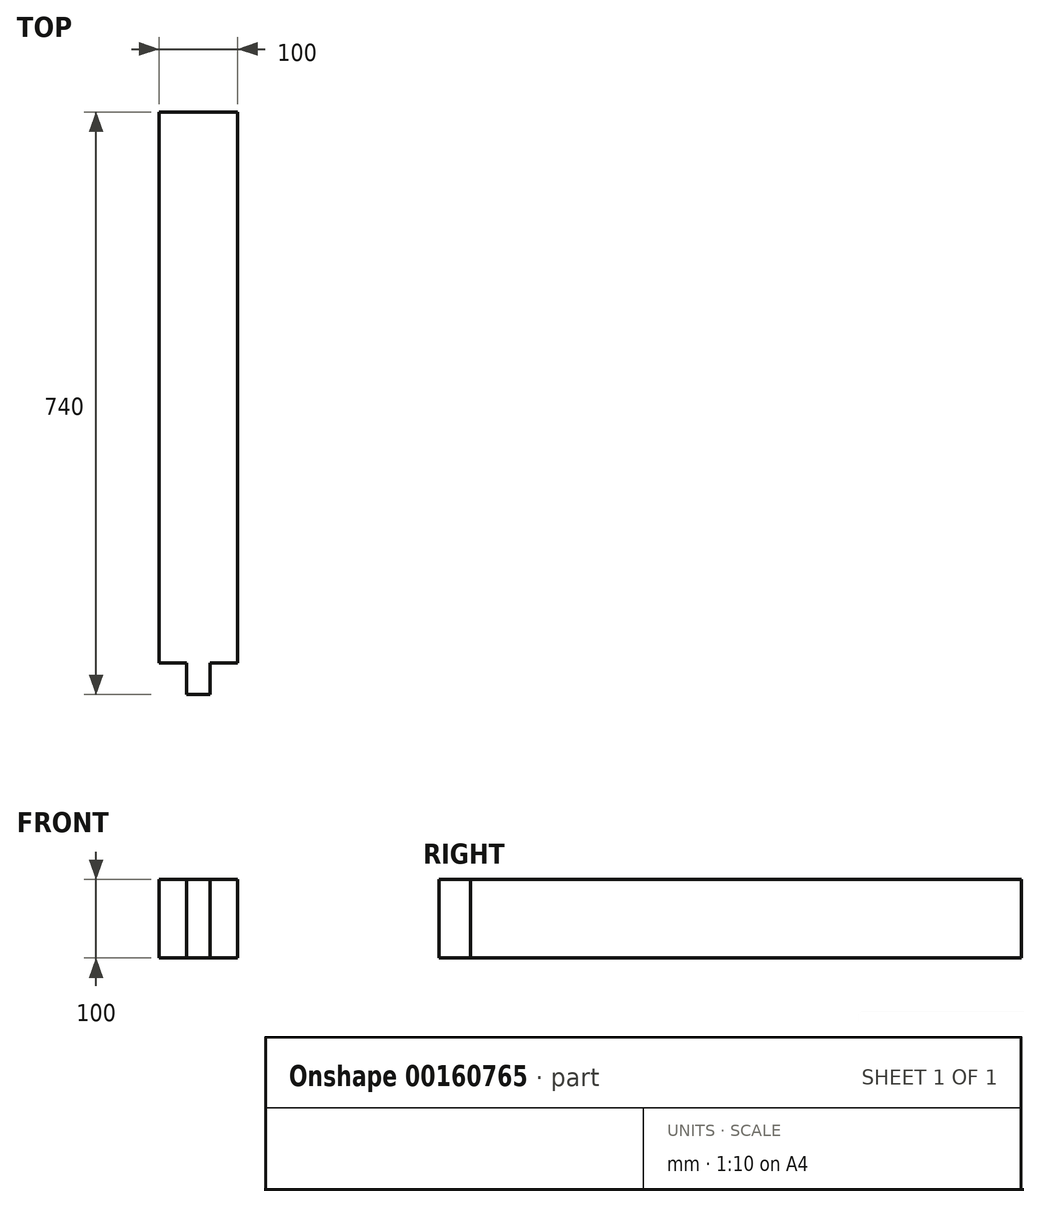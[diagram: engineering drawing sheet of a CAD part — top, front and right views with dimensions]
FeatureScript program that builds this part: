
annotation { "Feature Type Name" : "Feature", "Feature Type Description" : "" }
export const myFeature = defineFeature(function(context is Context, id is Id, definition is map)
    precondition{}
    {
        {
            assignVariable(context, id + "F0", {"name" : "L", "anyValue" : 600 * mm + 100 * mm});
        }
        {
            assignVariable(context, id + "F1", {"name" : "t_Feder", "anyValue" : 40 * mm});
        }
        {
            var Q0;
            Q0=qCreatedBy(makeId("Front.planeOp"),FACE);
            var sketch = newSketch(context, id + "F2", { "sketchPlane" : qUnion([Q0])});
            skLineSegment(sketch, "E0.bottom", {"start": v(50, -50) * mm, "end": v(-50, -50) * mm});
            skLineSegment(sketch, "E0.top", {"start": v(50, 50) * mm, "end": v(-50, 50) * mm});
            skLineSegment(sketch, "E0.left", {"start": v(50, -50) * mm, "end": v(50, 50) * mm});
            skLineSegment(sketch, "E0.right", {"start": v(-50, -50) * mm, "end": v(-50, 50) * mm});
            skPoint(sketch, "E0.middle", {"position": v(0, 0) * mm});
            skSolve(sketch);
        }
        {
            var Q0;
            Q0 = qSketchRegion(id + "F2", true);
            extrude(context, id + "F3", {"entities" : qUnion([Q0]), "endBound" : BoundingType.SYMMETRIC, "depth" : getVariable(context, 'L')});
        }
        {
            var Q0;
            Q0=makeQuery(id+"F3.opExtrude","CAP_FACE",FACE,{"disambiguationData":[OSD([sQuery(id+"F2.wireOp",EDGE,"E0.bottom"),sQuery(id+"F2.wireOp",EDGE,"E0.top"),sQuery(id+"F2.wireOp",EDGE,"E0.left"),sQuery(id+"F2.wireOp",EDGE,"E0.right")])],"isStart":false});
            var sketch = newSketch(context, id + "F4", { "sketchPlane" : qUnion([Q0])});
            skLineSegment(sketch, "E1", {"start": v(-50, 50) * mm, "end": v(50, -50) * mm, "construction": true});
            skLineSegment(sketch, "E2.bottom", {"start": v(15, 50) * mm, "end": v(-15, 50) * mm});
            skLineSegment(sketch, "E2.top", {"start": v(15, -50) * mm, "end": v(-15, -50) * mm});
            skLineSegment(sketch, "E2.left", {"start": v(15, 50) * mm, "end": v(15, -50) * mm});
            skLineSegment(sketch, "E2.right", {"start": v(-15, 50) * mm, "end": v(-15, -50) * mm});
            skPoint(sketch, "E2.middle", {"position": v(0, 0) * mm});
            skLineSegment(sketch, "E3", {"start": v(0, 50) * mm, "end": v(0, 0) * mm, "construction": true});
            skSolve(sketch);
        }
        {
            var Q0;
            Q0 = qSketchRegion(id + "F4", true);
            extrude(context, id + "F5", {"entities" : qUnion([Q0]), "operationType" : NewBodyOperationType.ADD, "depth" : getVariable(context, 't_Feder')});
        }
    });
